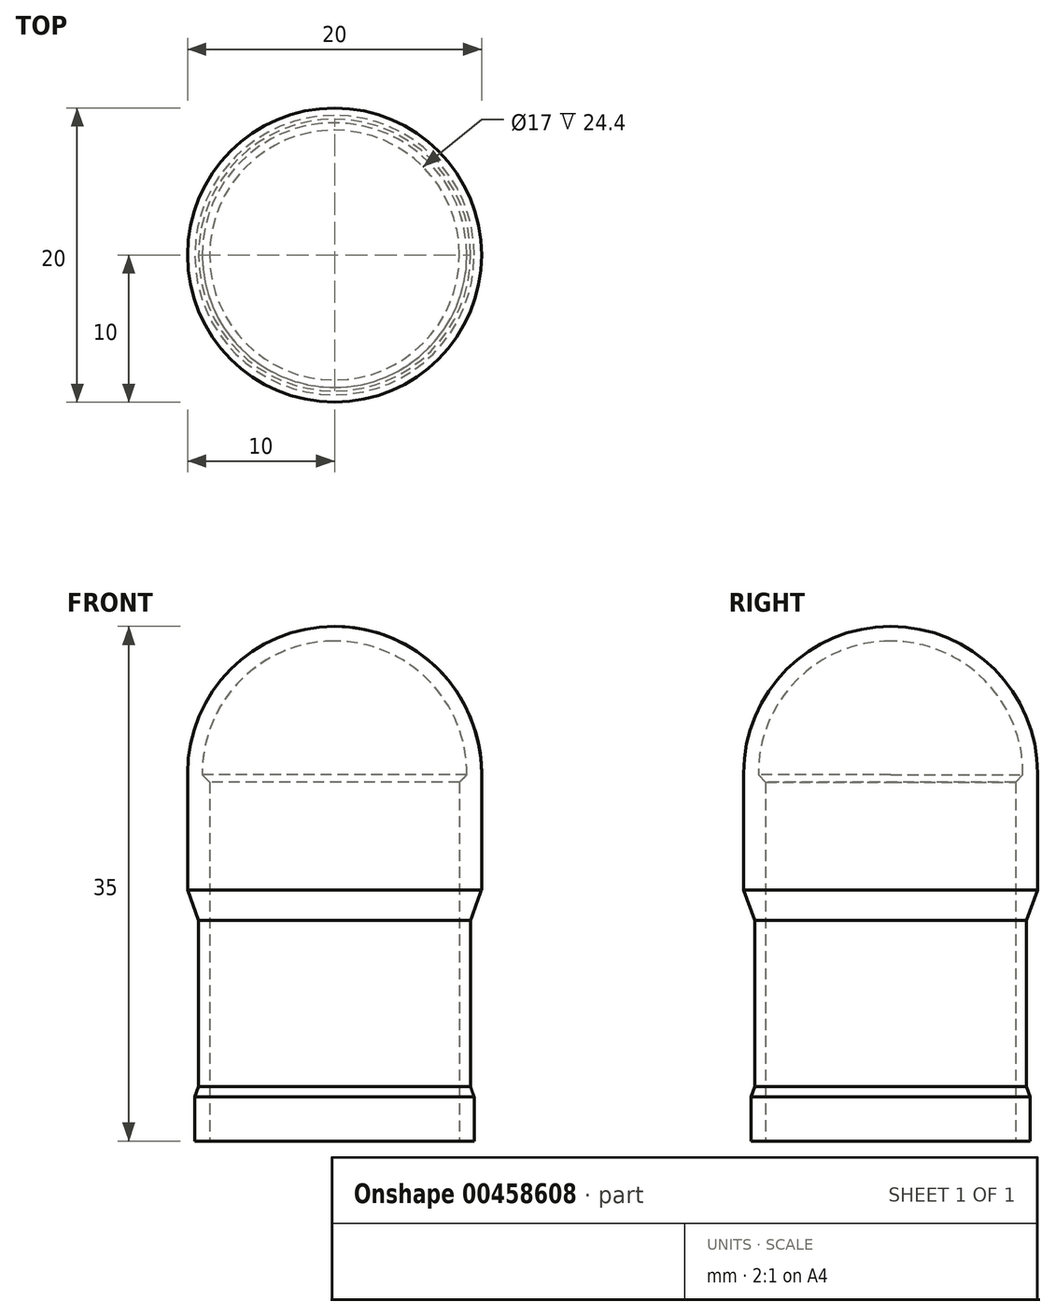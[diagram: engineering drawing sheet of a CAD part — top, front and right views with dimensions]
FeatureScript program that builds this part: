
annotation { "Feature Type Name" : "Feature", "Feature Type Description" : "" }
export const myFeature = defineFeature(function(context is Context, id is Id, definition is map)
    precondition{}
    {
        {
            var Q0;
            Q0=qCreatedBy(makeId("Top.planeOp"),FACE);
            var sketch = newSketch(context, id + "F0", { "sketchPlane" : qUnion([Q0])});
            skCircle(sketch, "E0", {"center": v(0, 0) * mm, "radius": 10 * mm});
            skCircle(sketch, "E1", {"center": v(0, 0) * mm, "radius": 8.5 * mm});
            skSolve(sketch);
        }
        {
            var Q0;
            Q0 = qSketchRegion(id + "F0", true);
            extrude(context, id + "F1", {"entities" : qUnion([Q0]), "depth" : 25 * mm, "offsetDistance" : 25 * mm});
        }
        {
            var Q0;
            Q0=qCreatedBy(makeId("Front.planeOp"),FACE);
            var sketch = newSketch(context, id + "F2", { "sketchPlane" : qUnion([Q0])});
            skArc(sketch, "E2", {"start": v(-10, 25) * mm, "mid": v(-7.07, 32.07) * mm, "end": v(0, 35) * mm});
            skLineSegment(sketch, "E3", {"start": v(0, 0) * mm, "end": v(0, 40.96) * mm, "construction": true});
            skArc(sketch, "E4", {"start": v(0, 34) * mm, "mid": v(-6.36, 31.36) * mm, "end": v(-9, 25) * mm});
            skLineSegment(sketch, "E5", {"start": v(0, 35) * mm, "end": v(0, 34) * mm});
            skLineSegment(sketch, "E6", {"start": v(-10, 25) * mm, "end": v(-9, 25) * mm});
            skSolve(sketch);
        }
        {
            var Q0;
            Q0 = qSketchRegion(id + "F2", true);
            var Q1;
            Q1=sQuery(id+"F2.wireOp",EDGE,"E3");
            revolve(context, id + "F3", {"operationType" : NewBodyOperationType.ADD, "surfaceOperationType" : NewSurfaceOperationType.NEW, "entities" : qUnion([Q0]), "axis" : qUnion([Q1]), "revolveType" : RevolveType.FULL});
        }
        {
            var Q0;
            Q0=qCreatedBy(makeId("Front.planeOp"),FACE);
            var sketch = newSketch(context, id + "F4", { "sketchPlane" : qUnion([Q0])});
            skLineSegment(sketch, "E7", {"start": v(0, 0) * mm, "end": v(0, 48.36) * mm, "construction": true});
            skLineSegment(sketch, "E8", {"start": v(-9.25, 3.69) * mm, "end": v(-9.25, 15) * mm});
            skLineSegment(sketch, "E9", {"start": v(-9.25, 15) * mm, "end": v(-10, 17.06) * mm});
            skLineSegment(sketch, "E10", {"start": v(-10, 17.06) * mm, "end": v(-11, 17.06) * mm});
            skLineSegment(sketch, "E11", {"start": v(-11, 17.06) * mm, "end": v(-11, 0) * mm});
            skLineSegment(sketch, "E12", {"start": v(-11, 0) * mm, "end": v(-9.5, 0) * mm});
            skLineSegment(sketch, "E13", {"start": v(-9.25, 3.69) * mm, "end": v(-9.5, 3) * mm});
            skLineSegment(sketch, "E14", {"start": v(-9.5, 3) * mm, "end": v(-9.5, 0) * mm});
            skPoint(sketch, "E15.orphan", {"position": v(-9.25, 0) * mm});
            skSolve(sketch);
        }
        {
            var Q0;
            Q0 = qSketchRegion(id + "F4", true);
            var Q1;
            Q1=sQuery(id+"F4.wireOp",EDGE,"E7");
            revolve(context, id + "F5", {"operationType" : NewBodyOperationType.REMOVE, "surfaceOperationType" : NewSurfaceOperationType.NEW, "entities" : qUnion([Q0]), "axis" : qUnion([Q1]), "revolveType" : RevolveType.FULL, "oppositeDirection" : true});
        }
        {
            var Q0;
            Q0=makeQuery(id+"F1.opExtrude","CAP_EDGE",EDGE,{"disambiguationData":[OSD([sQuery(id+"F0.wireOp",EDGE,"E1")])],"isStart":false});
            chamfer(context, id + "F6", {"entities" : qUnion([Q0]), "width" : 0.6 * mm, "tangentPropagation" : true});
        }
    });
